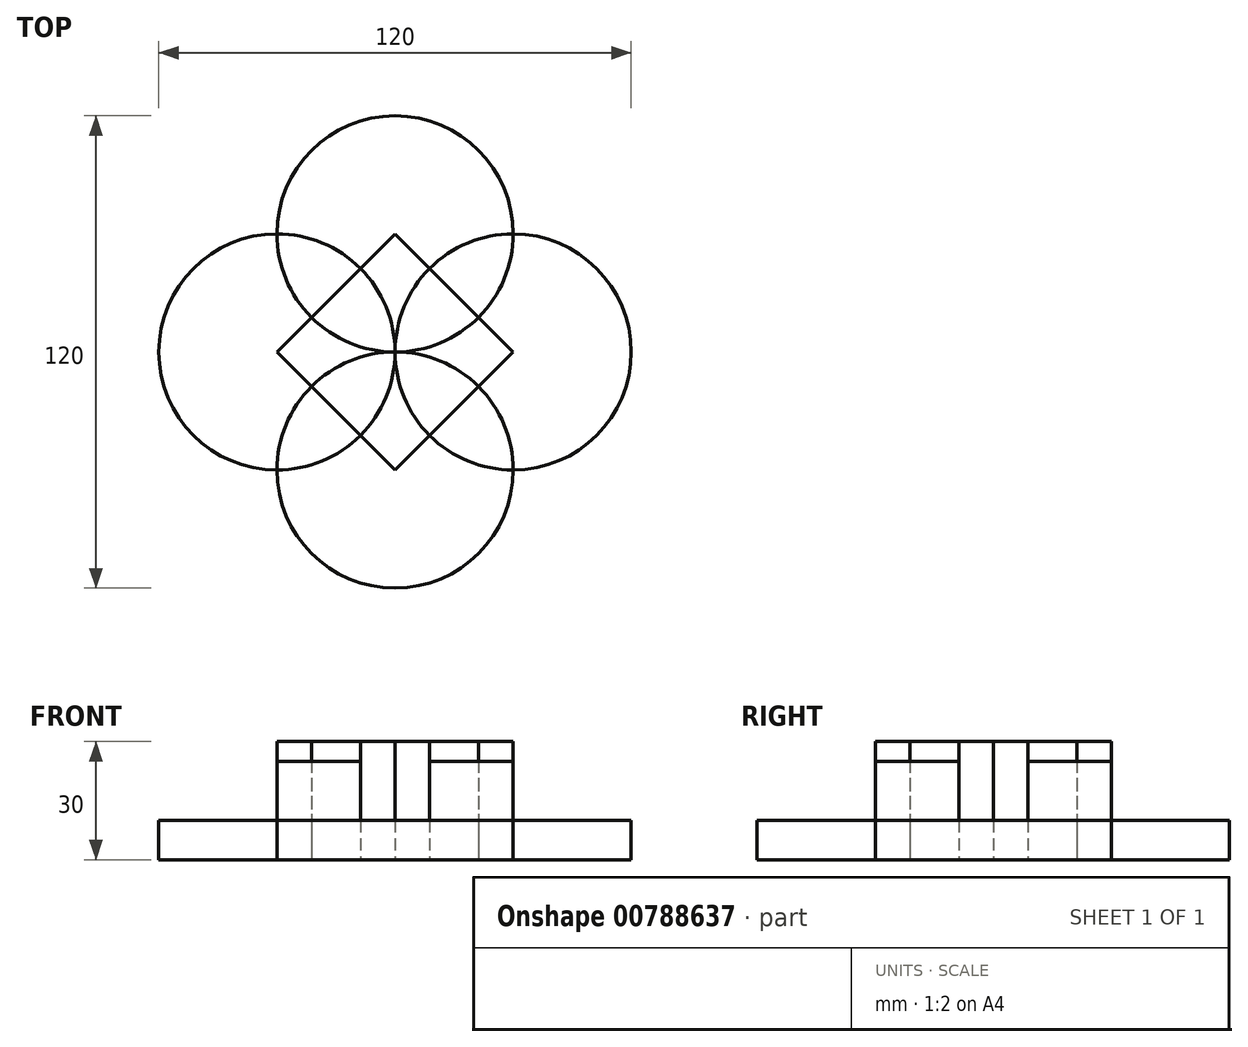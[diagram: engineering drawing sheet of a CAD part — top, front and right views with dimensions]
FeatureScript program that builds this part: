
annotation { "Feature Type Name" : "Feature", "Feature Type Description" : "" }
export const myFeature = defineFeature(function(context is Context, id is Id, definition is map)
    precondition{}
    {
        {
            var Q0;
            Q0=qCreatedBy(makeId("Top.planeOp"),FACE);
            var sketch = newSketch(context, id + "F0", { "sketchPlane" : qUnion([Q0])});
            skCircle(sketch, "E0", {"center": v(30, 0) * mm, "radius": 30 * mm});
            skCircle(sketch, "E1", {"center": v(0, 30) * mm, "radius": 30 * mm});
            skCircle(sketch, "E2", {"center": v(-30, 0) * mm, "radius": 30 * mm});
            skCircle(sketch, "E3", {"center": v(0, -30) * mm, "radius": 30 * mm});
            skPoint(sketch, "E4.converted.center.orphan", {"position": v(0, 0) * mm});
            skLineSegment(sketch, "E5", {"start": v(0, 30) * mm, "end": v(-30, 0) * mm});
            skLineSegment(sketch, "E6", {"start": v(0, -30) * mm, "end": v(-30, 0) * mm});
            skLineSegment(sketch, "E7", {"start": v(0, -30) * mm, "end": v(30, 0) * mm});
            skLineSegment(sketch, "E8", {"start": v(0, 30) * mm, "end": v(30, 0) * mm});
            skSolve(sketch);
        }
        {
            var Q0;
            {var subQ0=sQuery(id+"F0.wireOp",EDGE,"E3");var subQ1=sQuery(id+"F0.wireOp",EDGE,"E2");var subQ2=makeQuery(id+"F0.imprint","INTERSECT",VERTEX,{"derivedFrom":[subQ1,subQ0]});Q0=makeQuery(id+"F0.imprint","IMPRINT",FACE,{"disambiguationData":[TD([[makeQuery(id+"F0.imprint","IMPRINT",EDGE,{"disambiguationData":[TD([[subQ2,-1.0]])],"derivedFrom":subQ1}),1.0]])]});}
            var Q1;
            {var subQ0=sQuery(id+"F0.wireOp",EDGE,"E3");var subQ1=sQuery(id+"F0.wireOp",EDGE,"E0");var subQ2=makeQuery(id+"F0.imprint","INTERSECT",VERTEX,{"derivedFrom":[subQ1,subQ0]});Q1=makeQuery(id+"F0.imprint","IMPRINT",FACE,{"disambiguationData":[TD([[makeQuery(id+"F0.imprint","IMPRINT",EDGE,{"disambiguationData":[TD([[subQ2,1.0]])],"derivedFrom":subQ1}),1.0]])]});}
            var Q2;
            {var subQ0=sQuery(id+"F0.wireOp",EDGE,"E1");var subQ1=sQuery(id+"F0.wireOp",EDGE,"E0");var subQ2=makeQuery(id+"F0.imprint","INTERSECT",VERTEX,{"derivedFrom":[subQ1,subQ0]});Q2=makeQuery(id+"F0.imprint","IMPRINT",FACE,{"disambiguationData":[TD([[makeQuery(id+"F0.imprint","IMPRINT",EDGE,{"disambiguationData":[TD([[subQ2,-1.0]])],"derivedFrom":subQ1}),1.0]])]});}
            var Q3;
            {var subQ0=sQuery(id+"F0.wireOp",EDGE,"E2");var subQ1=sQuery(id+"F0.wireOp",EDGE,"E1");var subQ2=makeQuery(id+"F0.imprint","INTERSECT",VERTEX,{"derivedFrom":[subQ1,subQ0]});Q3=makeQuery(id+"F0.imprint","IMPRINT",FACE,{"disambiguationData":[TD([[makeQuery(id+"F0.imprint","IMPRINT",EDGE,{"disambiguationData":[TD([[subQ2,-1.0]])],"derivedFrom":subQ1}),1.0]])]});}
            extrude(context, id + "F1", {"entities" : qUnion([Q0, Q1, Q2, Q3]), "depth" : 25 * mm, "offsetDistance" : 25 * mm});
        }
        {
            var Q0;
            {var subQ0=sQuery(id+"F0.wireOp",EDGE,"E1");var subQ1=sQuery(id+"F0.wireOp",EDGE,"E0");var subQ2=makeQuery(id+"F0.imprint","INTERSECT",VERTEX,{"derivedFrom":[subQ1,subQ0]});Q0=makeQuery(id+"F0.imprint","IMPRINT",FACE,{"disambiguationData":[TD([[makeQuery(id+"F0.imprint","IMPRINT",EDGE,{"disambiguationData":[TD([[subQ2,1.0]])],"derivedFrom":subQ1}),1.0]])]});}
            var Q1;
            {var subQ0=sQuery(id+"F0.wireOp",EDGE,"E3");var subQ1=sQuery(id+"F0.wireOp",EDGE,"E0");var subQ2=makeQuery(id+"F0.imprint","INTERSECT",VERTEX,{"derivedFrom":[subQ1,subQ0]});Q1=makeQuery(id+"F0.imprint","IMPRINT",FACE,{"disambiguationData":[TD([[makeQuery(id+"F0.imprint","IMPRINT",EDGE,{"disambiguationData":[TD([[subQ2,1.0]])],"derivedFrom":subQ0}),1.0]])]});}
            var Q2;
            {var subQ0=sQuery(id+"F0.wireOp",EDGE,"E2");var subQ1=sQuery(id+"F0.wireOp",EDGE,"E1");var subQ2=makeQuery(id+"F0.imprint","INTERSECT",VERTEX,{"derivedFrom":[subQ1,subQ0]});Q2=makeQuery(id+"F0.imprint","IMPRINT",FACE,{"disambiguationData":[TD([[makeQuery(id+"F0.imprint","IMPRINT",EDGE,{"disambiguationData":[TD([[subQ2,-1.0]])],"derivedFrom":subQ0}),1.0]])]});}
            var Q3;
            {var subQ0=sQuery(id+"F0.wireOp",EDGE,"E1");var subQ1=sQuery(id+"F0.wireOp",EDGE,"E0");var subQ2=makeQuery(id+"F0.imprint","INTERSECT",VERTEX,{"derivedFrom":[subQ1,subQ0]});Q3=makeQuery(id+"F0.imprint","IMPRINT",FACE,{"disambiguationData":[TD([[makeQuery(id+"F0.imprint","IMPRINT",EDGE,{"disambiguationData":[TD([[subQ2,-1.0]])],"derivedFrom":subQ0}),1.0]])]});}
            extrude(context, id + "F2", {"entities" : qUnion([Q0, Q1, Q2, Q3]), "depth" : 10 * mm, "offsetDistance" : 25 * mm});
        }
        {
            var Q0;
            {var subQ0=sQuery(id+"F0.wireOp",EDGE,"E8");var subQ5=sQuery(id+"F0.wireOp",EDGE,"E5");var subQ7=makeQuery(id+"F0.imprint","INTERSECT",VERTEX,{"derivedFrom":[subQ5,subQ0]});Q0=makeQuery(id+"F0.imprint","IMPRINT",FACE,{"disambiguationData":[TD([[makeQuery(id+"F0.imprint","IMPRINT",EDGE,{"disambiguationData":[TD([[subQ7,-1.0]])],"derivedFrom":subQ5}),1.0]])]});}
            var Q1;
            {var subQ0=sQuery(id+"F0.wireOp",EDGE,"E7");var subQ5=sQuery(id+"F0.wireOp",EDGE,"E6");var subQ7=makeQuery(id+"F0.imprint","INTERSECT",VERTEX,{"derivedFrom":[subQ5,subQ0]});Q1=makeQuery(id+"F0.imprint","IMPRINT",FACE,{"disambiguationData":[TD([[makeQuery(id+"F0.imprint","IMPRINT",EDGE,{"disambiguationData":[TD([[subQ7,-1.0]])],"derivedFrom":subQ5}),-1.0]])]});}
            var Q2;
            {var subQ0=sQuery(id+"F0.wireOp",EDGE,"E5");var subQ5=sQuery(id+"F0.wireOp",EDGE,"E6");var subQ7=makeQuery(id+"F0.imprint","INTERSECT",VERTEX,{"derivedFrom":[subQ0,subQ5]});Q2=makeQuery(id+"F0.imprint","IMPRINT",FACE,{"disambiguationData":[TD([[makeQuery(id+"F0.imprint","IMPRINT",EDGE,{"disambiguationData":[TD([[subQ7,1.0]])],"derivedFrom":subQ0}),1.0]])]});}
            var Q3;
            {var subQ0=sQuery(id+"F0.wireOp",EDGE,"E8");var subQ5=sQuery(id+"F0.wireOp",EDGE,"E7");var subQ6=makeQuery(id+"F0.imprint","INTERSECT",VERTEX,{"derivedFrom":[subQ5,subQ0]});Q3=makeQuery(id+"F0.imprint","IMPRINT",FACE,{"disambiguationData":[TD([[makeQuery(id+"F0.imprint","IMPRINT",EDGE,{"disambiguationData":[TD([[subQ6,1.0]])],"derivedFrom":subQ5}),1.0]])]});}
            extrude(context, id + "F3", {"entities" : qUnion([Q0, Q1, Q2, Q3]), "depth" : 30 * mm, "offsetDistance" : 25 * mm});
        }
    });
